# Revit family: QSP1
name_source: partatom
category: Lighting Fixtures
units: mm (PartAtom-declared; Revit-internal decimal feet)

## family parameters
Cut with Voids When Loaded = No
Host = Face
Light Source = Yes
OmniClass Number = 23.80.70.11
OmniClass Title = Luminaries for Internal Lighting
Part Type = Normal
Room Calculation Point = No
Round Connector Dimension = Use Diameter
Shared = No

## types (5) — shared parameters
Apparent Load = 0 VA
Color Filter = 16777215
Default Elevation = 48"
Description = Architectural wallpack in two stylish shapes.
Dimming Lamp Color Temperature Shift = <None>
Emit Shape Visible in Rendering = No
Emit from Circle Diameter = 6"
Lamp = LED
Load Classification = Lighting
Manufacturer = Beacon
Model = QSP1
Opal lens = Etched Glass
Photometric Web File = RDI 42F WT TRP RTP QSP.ies
Tilt Angle = -90.00°
URL = https://www.currentlighting.com
Voltage = 120 V
Wattage Comments = 15W/20W/30W

## per-type parameters (varying)
| type | Finish |
| QSP PS | Platinum |
| QSP BK | Black |
| QSP GR | Gray |
| QSP WH | White |
| QSP DB | Bronze |

## geometry (parser evidence)
native form markers: Sweep x1
no freeform markers — native parametric forms only
